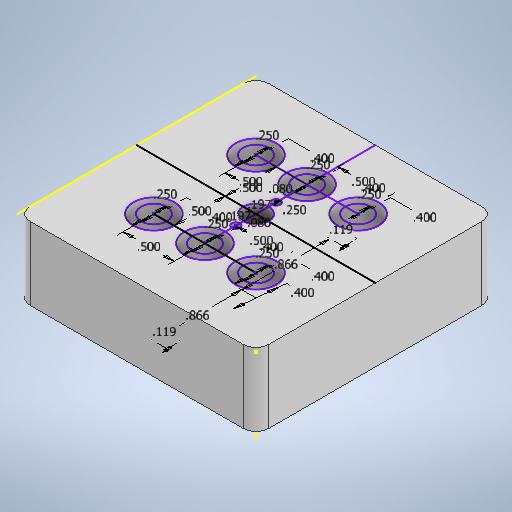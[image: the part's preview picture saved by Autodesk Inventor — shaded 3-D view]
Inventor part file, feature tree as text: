
AUTODESK INVENTOR PART (.ipt)
format: ipt  version: 2025.2 (Build 292293000, 293)  size: 331,264 bytes
history: native  units: in
note: dims shown in document units (in); Inventor stores cm internally (conversion verified against a paired STEP export)
features: extrude x6, sketch x3, fillet x1
ambient origin geometry x8: Origin, YZ Plane, XZ Plane, XY Plane, X Axis, Y Axis, Z Axis, Center Point
bodies: Solid1 (feature_tree)
feature tree (10):
  extrude  "Extrusion1"  Depth=2.3386in
  sketch  "Sketch2"  dims[d2=0.7126in d3=0.0in d4=0.5in]
  extrude  "Extrusion2"  Depth=0.7126in
  extrude  "Extrusion3"  Depth=0.125in
  extrude  "Extrusion4"  Depth=0.125in
  sketch  "Sketch3"  dims[d5=0.4in d6=0.5in d7=0.5in d8=0.4in d9=0.4in d10=0.5in d11=0.4in d12=0.5in d13=0.5in d14=0.4in d15=0.4in d16=0.25in d17=0.25in d18=0.25in d19=0.25in d20=0.25in d21=0.25in d22=0.25in d23=0.197in d24=0.197in d25=0.0797in d26=0.0797in d27=1.5in d28=0.0in d29=0.3in d30=0.0in d31=0.175in d32=0.0in d33=0.8661in d34=0.8661in d35=0.1191in d36=0.1191in d37=0.4in d38=0.175in d39=0.0in d40=0.3in d41=0.0in d42=0.125in]
  extrude  "Extrusion5"  Depth=0.125in
  extrude  "Extrusion6"  Depth=0.125in
  fillet  "Fillet1"  Radius=0.5in
  sketch  "Sketch1"  dims[d0=2.3386in d1=2.3386in]
